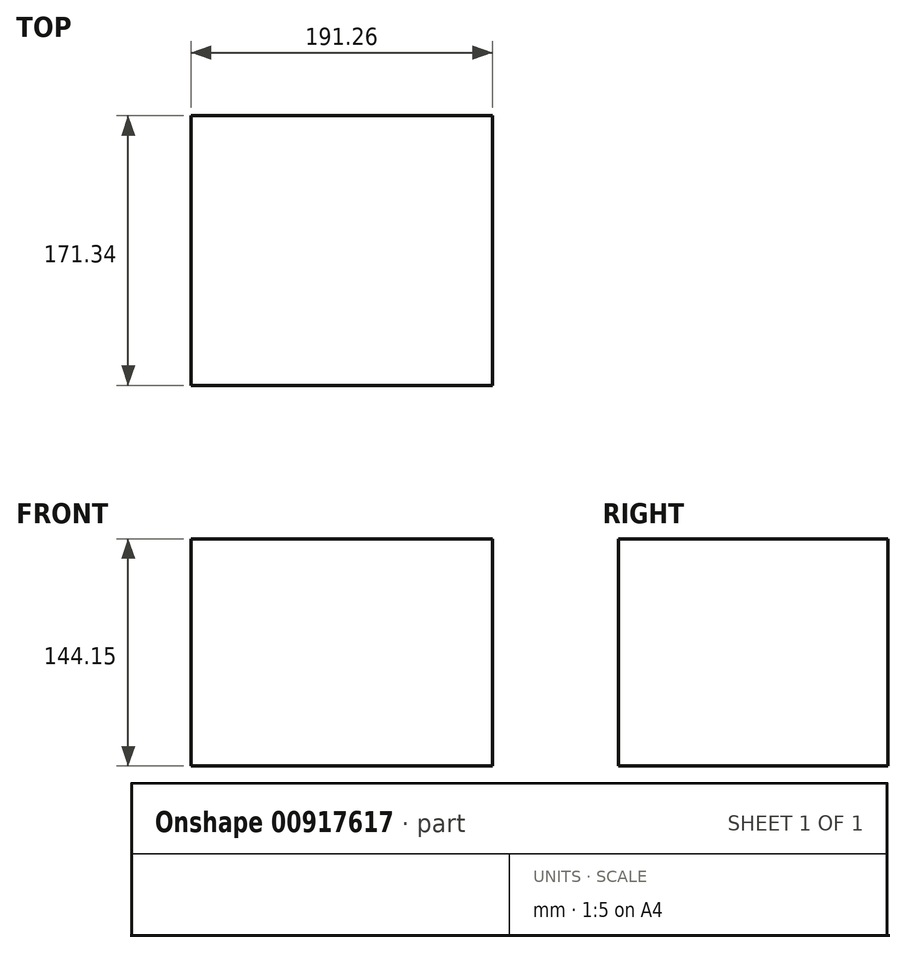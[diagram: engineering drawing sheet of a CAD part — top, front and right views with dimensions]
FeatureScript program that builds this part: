
annotation { "Feature Type Name" : "Feature", "Feature Type Description" : "" }
export const myFeature = defineFeature(function(context is Context, id is Id, definition is map)
    precondition{}
    {
        {
            var Q0;
            Q0=qCreatedBy(makeId("Top.planeOp"),FACE);
            var sketch = newSketch(context, id + "F0", { "sketchPlane" : qUnion([Q0])});
            skLineSegment(sketch, "E0.bottom", {"start": v(-91.98, -86.87) * mm, "end": v(99.28, -86.87) * mm});
            skLineSegment(sketch, "E0.top", {"start": v(-91.98, 84.47) * mm, "end": v(99.28, 84.47) * mm});
            skLineSegment(sketch, "E0.left", {"start": v(-91.98, -86.87) * mm, "end": v(-91.98, 84.47) * mm});
            skLineSegment(sketch, "E0.right", {"start": v(99.28, -86.87) * mm, "end": v(99.28, 84.47) * mm});
            skSolve(sketch);
        }
        {
            var Q0;
            Q0=makeQuery(id+"F0.imprint","IMPRINT",FACE,{"disambiguationData":[TD([[makeQuery(id+"F0.imprint","IMPRINT",EDGE,{"derivedFrom":sQuery(id+"F0.wireOp",EDGE,"E0.bottom")}),1.0]])]});
            extrude(context, id + "F1", {"entities" : qUnion([Q0]), "depth" : 144.15 * mm, "offsetDistance" : 25 * mm});
        }
    });
